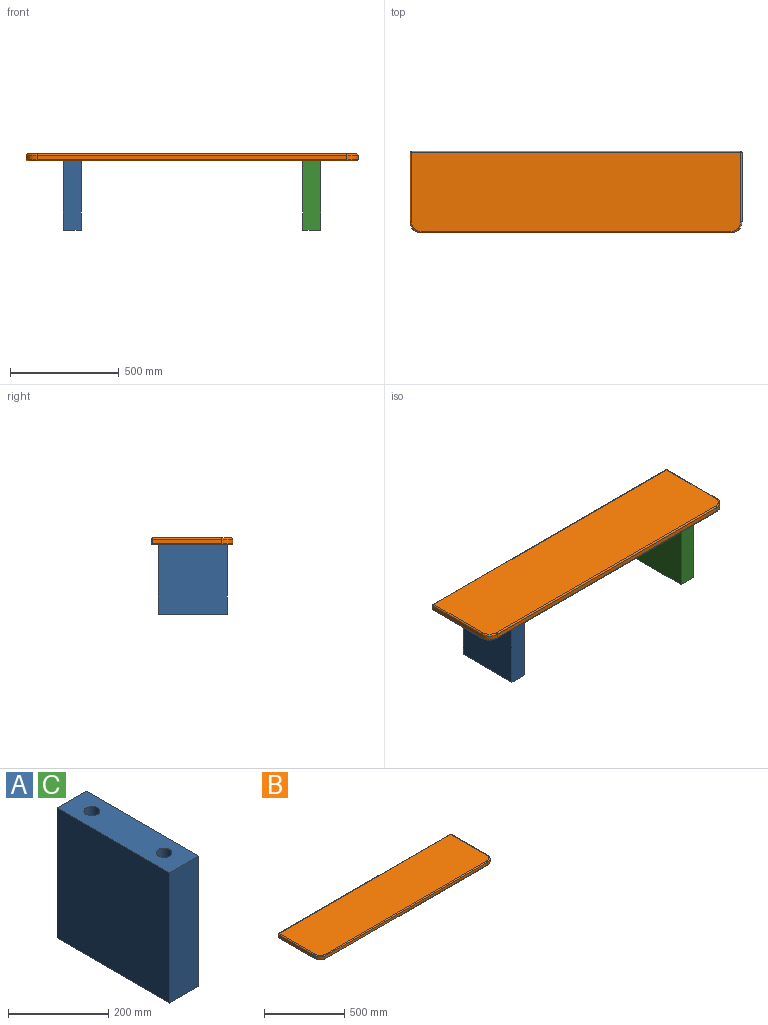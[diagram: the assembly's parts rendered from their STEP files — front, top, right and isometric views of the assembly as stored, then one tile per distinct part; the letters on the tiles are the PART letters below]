
ASSEMBLY  parts=3 mates=1
PART A: 10 faces, bbox 82.6x317.5x317.5 mm
  f0: plane 317.5x82.55mm, normal (0,0,1), area 24626.2mm2, adj f1,f3,f4,f5,f7,f9
  f1: plane 317.5x82.55mm, normal (0,-1,0), area 26209.6mm2, adj f0,f2,f4,f5
  f2: plane 317.5x82.55mm, normal (0,0,-1), area 26209.6mm2, adj f1,f3,f4,f5
  f3: plane 317.5x82.55mm, normal (0,1,0), area 26209.6mm2, adj f0,f2,f4,f5
  f4: plane 317.5x317.5mm, normal (1,0,0), area 100806.2mm2, adj f0,f1,f2,f3
  f5: plane 317.5x317.5mm, normal (-1,0,0), area 100806.2mm2, adj f0,f1,f2,f3
  f6: cone r=0mm half-angle=59deg, axis (0,0,1), area 923.7mm2, adj f7
  f7: cylinder r=15.88mm len=50.8mm, axis (0,0,1), area 5067.1mm2, adj f0,f6
  f8: cone r=0mm half-angle=59deg, axis (0,0,1), area 923.7mm2, adj f9
  f9: cylinder r=15.88mm len=50.8mm, axis (0,0,1), area 5067.1mm2, adj f0,f8
PART B: 34 faces, bbox 1532.4x378.8x31.8 mm
  f0: cylinder r=15.88mm len=31.75mm, axis (0,0,-1), area 2533.5mm2, adj f1,f9
  f1: plane 31.75x31.75mm, normal (0,0,-1), area 791.7mm2, adj f0
  f2: cylinder r=15.88mm len=31.75mm, axis (0,0,-1), area 2533.5mm2, adj f3,f9
  f3: plane 31.75x31.75mm, normal (0,0,-1), area 791.7mm2, adj f2
  f4: plane 1511.3x19.05mm, normal (0,1,0), area 28790.3mm2, adj f18,f19,f24,f25
  f5: plane 317.5x19.05mm, normal (-1,0,0), area 6048.4mm2, adj f10,f17,f24,f29
  f6: plane 1422.4x19.05mm, normal (0,-1,0), area 27096.7mm2, adj f10,f11,f13,f26
  f7: plane 317.5x19.05mm, normal (1,0,0), area 6048.4mm2, adj f11,f14,f19,f20
  f8: plane 1511.3x361.95mm, normal (0,0,1), area 546167mm2, adj f20,f23,f25,f26,f28,f29
  f9: plane 1511.3x361.95mm, normal (0,0,-1), area 543000.1mm2, adj f0,f2,f12,f13,f14,f15,f17,f18
  f10: cylinder r=50.8mm len=50.8mm, axis (0,0,-1), area 1520.1mm2, adj f5,f6,f15,f28
  f11: cylinder r=50.8mm len=50.8mm, axis (0,0,1), area 1520.1mm2, adj f6,f7,f12,f23
  f12: torus R=44.45mm, axis (0,0,1), area 759.8mm2, adj f9,f11,f13,f14
  f13: cylinder r=6.35mm len=1422.4mm, axis (1,0,0), area 14187.8mm2, adj f6,f9,f12,f15
  f14: cylinder r=6.35mm len=317.5mm, axis (0,1,0), area 3166.9mm2, adj f7,f9,f12,f16
  f15: torus R=44.45mm, axis (0,0,1), area 759.8mm2, adj f9,f10,f13,f17
  f16: sphere r=6.35mm, area 63.3mm2, adj f14,f18,f19
  f17: cylinder r=6.35mm len=317.5mm, axis (0,-1,0), area 3166.9mm2, adj f5,f9,f15,f21
  f18: cylinder r=6.35mm len=1511.3mm, axis (-1,0,0), area 15074.5mm2, adj f4,f9,f16,f21
  f19: cylinder r=6.35mm len=19.05mm, axis (0,0,-1), area 190mm2, adj f4,f7,f16,f22
  f20: cylinder r=6.35mm len=317.5mm, axis (0,-1,0), area 3166.9mm2, adj f7,f8,f22,f23
  f21: sphere r=6.35mm, area 63.3mm2, adj f17,f18,f24
  f22: sphere r=6.35mm, area 63.3mm2, adj f19,f20,f25
  f23: torus R=44.45mm, axis (0,0,1), area 759.8mm2, adj f8,f11,f20,f26
  f24: cylinder r=6.35mm len=19.05mm, axis (0,0,1), area 190mm2, adj f4,f5,f21,f27
  f25: cylinder r=6.35mm len=1511.3mm, axis (1,0,0), area 15074.5mm2, adj f4,f8,f22,f27
  f26: cylinder r=6.35mm len=1422.4mm, axis (-1,0,0), area 14187.8mm2, adj f6,f8,f23,f28
  f27: sphere r=6.35mm, area 63.3mm2, adj f24,f25,f29
  f28: torus R=44.45mm, axis (0,0,1), area 759.8mm2, adj f8,f10,f26,f29
  f29: cylinder r=6.35mm len=317.5mm, axis (0,1,0), area 3166.9mm2, adj f5,f8,f27,f28
  f30: cylinder r=15.88mm len=31.75mm, axis (0,0,-1), area 2533.5mm2, adj f9,f31
  f31: plane 31.75x31.75mm, normal (0,0,-1), area 791.7mm2, adj f30
  f32: cylinder r=15.88mm len=31.75mm, axis (0,0,-1), area 2533.5mm2, adj f9,f33
  f33: plane 31.75x31.75mm, normal (0,0,-1), area 791.7mm2, adj f32
PART C: same geometry as A
PLACE A t=(-1098.55,0,0)mm
PLACE B at identity fixed
PLACE C at identity
MATE fastened B.f0 <-> A.f8  axis (0,0,-1) through (-549.28,82.55,0)mm
